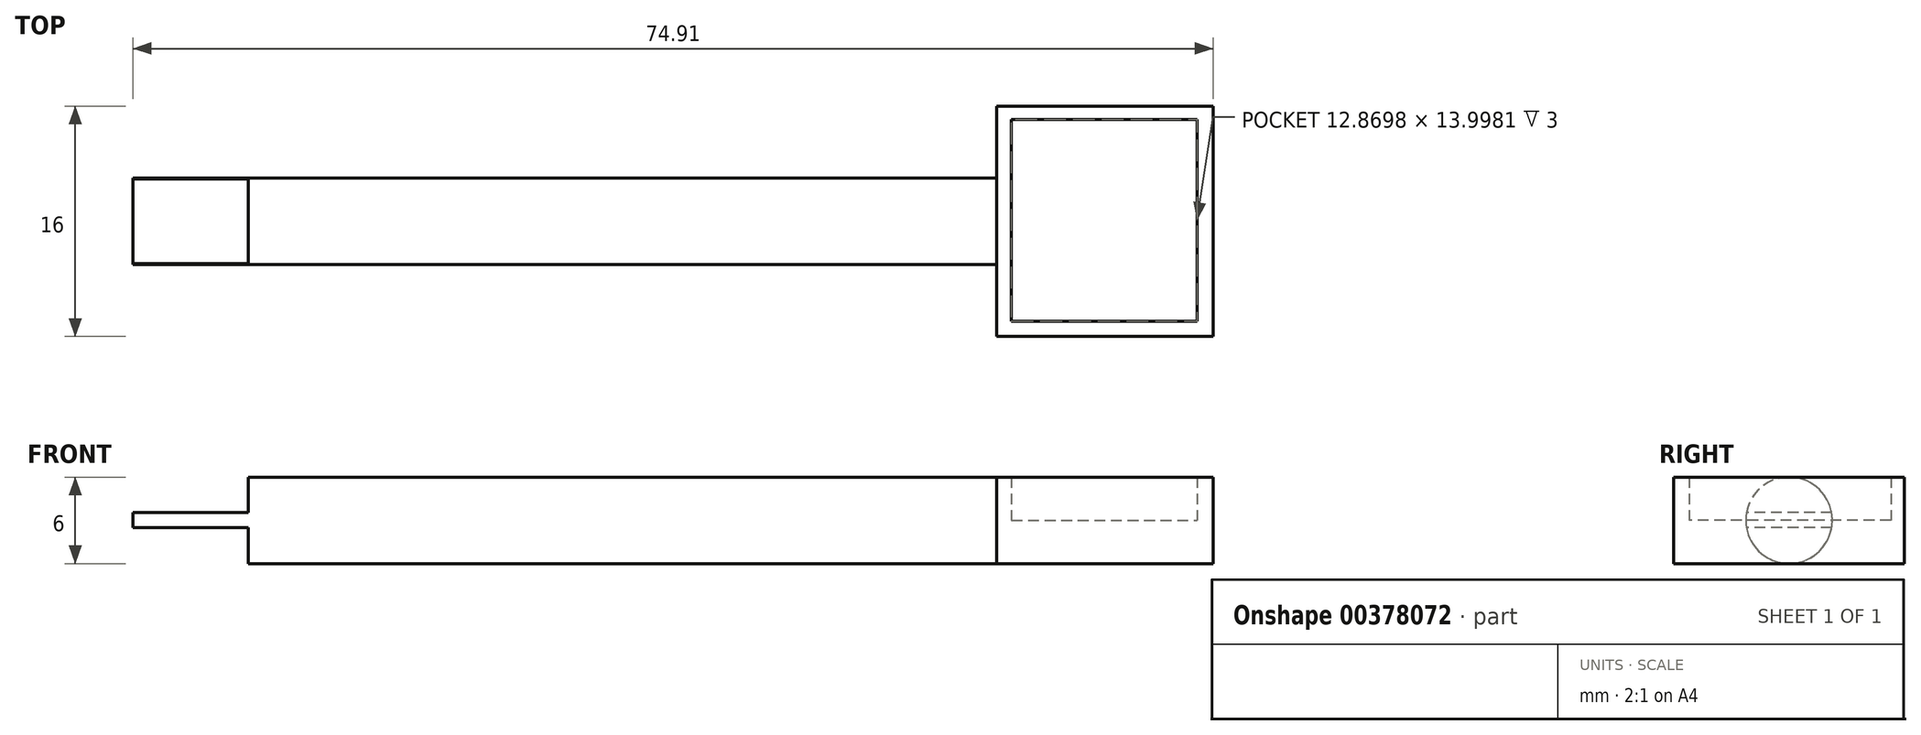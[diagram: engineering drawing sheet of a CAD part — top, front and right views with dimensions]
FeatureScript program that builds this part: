
annotation { "Feature Type Name" : "Feature", "Feature Type Description" : "" }
export const myFeature = defineFeature(function(context is Context, id is Id, definition is map)
    precondition{}
    {
        {
            var Q0;
            Q0=qCreatedBy(makeId("Front.planeOp"),FACE);
            var sketch = newSketch(context, id + "F0", { "sketchPlane" : qUnion([Q0])});
            skLineSegment(sketch, "E0.bottom", {"start": v(0, 3) * mm, "end": v(30, 3) * mm});
            skLineSegment(sketch, "E0.top", {"start": v(0, 0) * mm, "end": v(30, 0) * mm});
            skLineSegment(sketch, "E0.right", {"start": v(30, 3) * mm, "end": v(30, 0) * mm});
            skLineSegment(sketch, "E1.bottom", {"start": v(0, 3) * mm, "end": v(-30, 3) * mm});
            skLineSegment(sketch, "E1.top", {"start": v(0, 0) * mm, "end": v(-30, 0) * mm});
            skLineSegment(sketch, "E1.right", {"start": v(-30, 3) * mm, "end": v(-30, 0) * mm});
            skSolve(sketch);
        }
        {
            var Q0;
            Q0=makeQuery(id+"F0.imprint","IMPRINT",FACE,{"disambiguationData":[TD([[makeQuery(id+"F0.imprint","IMPRINT",EDGE,{"derivedFrom":sQuery(id+"F0.wireOp",EDGE,"E0.bottom")}),-1.0]])]});
            var Q1;
            Q1=sQuery(id+"F0.wireOp",EDGE,"E0.top");
            revolve(context, id + "F1", {"entities" : qUnion([Q0]), "axis" : qUnion([Q1]), "revolveType" : RevolveType.FULL});
        }
        {
            var Q0;
            Q0=makeQuery(id+"F1.opRevolve","SWEPT_FACE",FACE,{"disambiguationData":[OSD([sQuery(id+"F0.wireOp",EDGE,"E1.right")])]});
            var sketch = newSketch(context, id + "F2", { "sketchPlane" : qUnion([Q0])});
            skArc(sketch, "E2", {"start": v(-3, -0.5) * mm, "mid": v(0, -3.05) * mm, "end": v(3, -0.5) * mm});
            skLineSegment(sketch, "E3", {"start": v(-3, 0.54) * mm, "end": v(3, 0.54) * mm});
            skLineSegment(sketch, "E4", {"start": v(-3, -0.5) * mm, "end": v(3, -0.5) * mm});
            skArc(sketch, "E5.trimOffspring", {"start": v(3, 0.54) * mm, "mid": v(0, 3.05) * mm, "end": v(-3, 0.54) * mm});
            skSolve(sketch);
        }
        {
            var Q0;
            Q0 = qSketchRegion(id + "F2", true);
            extrude(context, id + "F3", {"entities" : qUnion([Q0]), "operationType" : NewBodyOperationType.REMOVE, "oppositeDirection" : true, "depth" : 8 * mm});
        }
        {
            var Q0;
            Q0=qCreatedBy(makeId("Top.planeOp"),FACE);
            var sketch = newSketch(context, id + "F4", { "sketchPlane" : qUnion([Q0])});
            skLineSegment(sketch, "E6", {"start": v(29.91, 0) * mm, "end": v(29.91, 8) * mm});
            skLineSegment(sketch, "E7", {"start": v(29.91, 8) * mm, "end": v(44.91, 8) * mm});
            skLineSegment(sketch, "E8", {"start": v(29.91, 0) * mm, "end": v(29.91, -8) * mm});
            skLineSegment(sketch, "E9", {"start": v(29.91, -8) * mm, "end": v(44.91, -8) * mm});
            skLineSegment(sketch, "E10", {"start": v(44.91, 8) * mm, "end": v(44.91, -8) * mm});
            skLineSegment(sketch, "E11.bottom", {"start": v(30.94, 7.07) * mm, "end": v(43.8, 7.07) * mm});
            skLineSegment(sketch, "E11.top", {"start": v(30.94, -6.93) * mm, "end": v(43.8, -6.93) * mm});
            skLineSegment(sketch, "E11.left", {"start": v(30.94, 7.07) * mm, "end": v(30.94, -6.93) * mm});
            skLineSegment(sketch, "E11.right", {"start": v(43.8, 7.07) * mm, "end": v(43.8, -6.93) * mm});
            skSolve(sketch);
        }
        {
            var Q0;
            Q0=makeQuery(id+"F4.imprint","IMPRINT",FACE,{"disambiguationData":[TD([[makeQuery(id+"F4.imprint","IMPRINT",EDGE,{"derivedFrom":sQuery(id+"F4.wireOp",EDGE,"E11.bottom")}),-1.0]])]});
            var Q1;
            Q1=makeQuery(id+"F4.imprint","IMPRINT",FACE,{"disambiguationData":[TD([[makeQuery(id+"F4.imprint","IMPRINT",EDGE,{"derivedFrom":sQuery(id+"F4.wireOp",EDGE,"E6")}),-1.0]])]});
            var Q2;
            Q2=sQuery(id+"F4.wireOp",EDGE,"E7");
            var Q3;
            Q3=sQuery(id+"F4.wireOp",EDGE,"E10");
            var Q4;
            Q4=sQuery(id+"F4.wireOp",EDGE,"E9");
            extrude(context, id + "F5", {"entities" : qUnion([Q0, Q1]), "operationType" : NewBodyOperationType.ADD, "surfaceEntities" : qUnion([Q2, Q3, Q4]), "oppositeDirection" : true, "depth" : 3 * mm});
        }
        {
            var Q0;
            Q0 = qSketchRegion(id + "F4", true);
            extrude(context, id + "F6", {"entities" : qUnion([Q0]), "operationType" : NewBodyOperationType.ADD, "depth" : 3 * mm});
        }
    });
